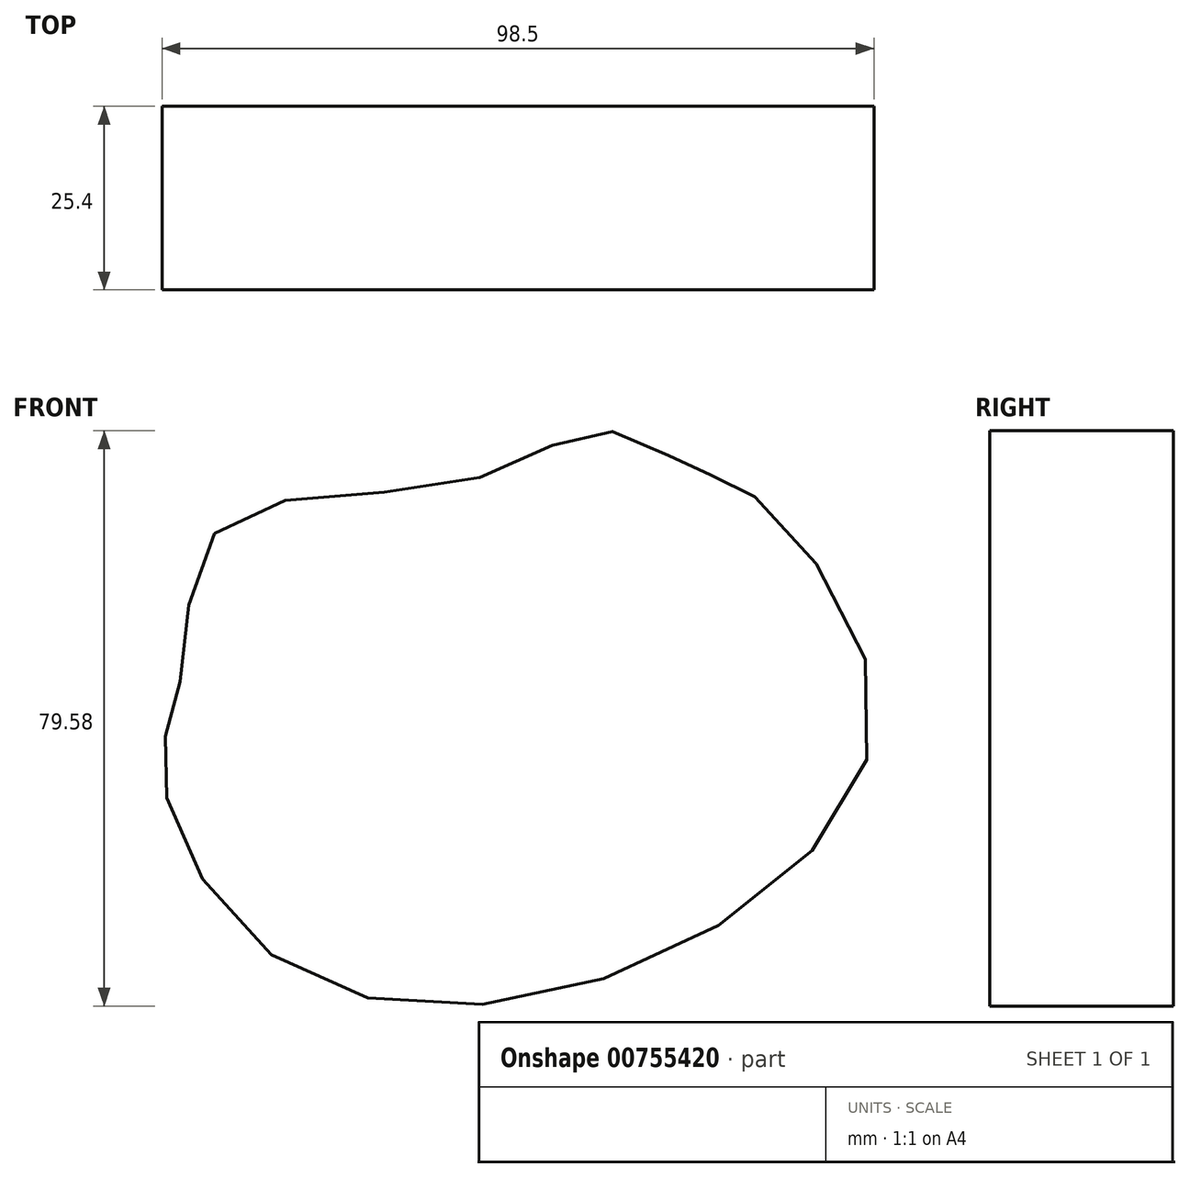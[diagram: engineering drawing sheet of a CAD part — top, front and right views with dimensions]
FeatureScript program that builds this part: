
annotation { "Feature Type Name" : "Feature", "Feature Type Description" : "" }
export const myFeature = defineFeature(function(context is Context, id is Id, definition is map)
    precondition{}
    {
        {
            var Q0;
            Q0=qCreatedBy(makeId("Front.planeOp"),FACE);
            var sketch = newSketch(context, id + "F0", { "sketchPlane" : qUnion([Q0])});
            skFitSpline(sketch, "E0", {"points": [v(-50.88, 7.71) * mm, v(-53.37, -4.62) * mm, v(-35.95, -31.67) * mm, v(14.93, -30.53) * mm, v(45.08, 4.16) * mm, v(26.82, 34.57) * mm, v(20.19, 37.08) * mm, v(8.02, 42.41) * mm, v(-11.9, 35.28) * mm, v(-45.08, 29.3) * mm, v(-50.88, 7.71) * mm]});
            skSolve(sketch);
        }
        {
            var Q0;
            Q0=makeQuery(id+"F0.imprint","IMPRINT",FACE,{"disambiguationData":[TD([[makeQuery(id+"F0.imprint","IMPRINT",EDGE,{"derivedFrom":sQuery(id+"F0.wireOp",EDGE,"E0")}),1.0]])]});
            extrude(context, id + "F1", {"entities" : qUnion([Q0]), "oppositeDirection" : true, "depth" : 25.4 * mm, "offsetDistance" : 25.4 * mm});
        }
    });
